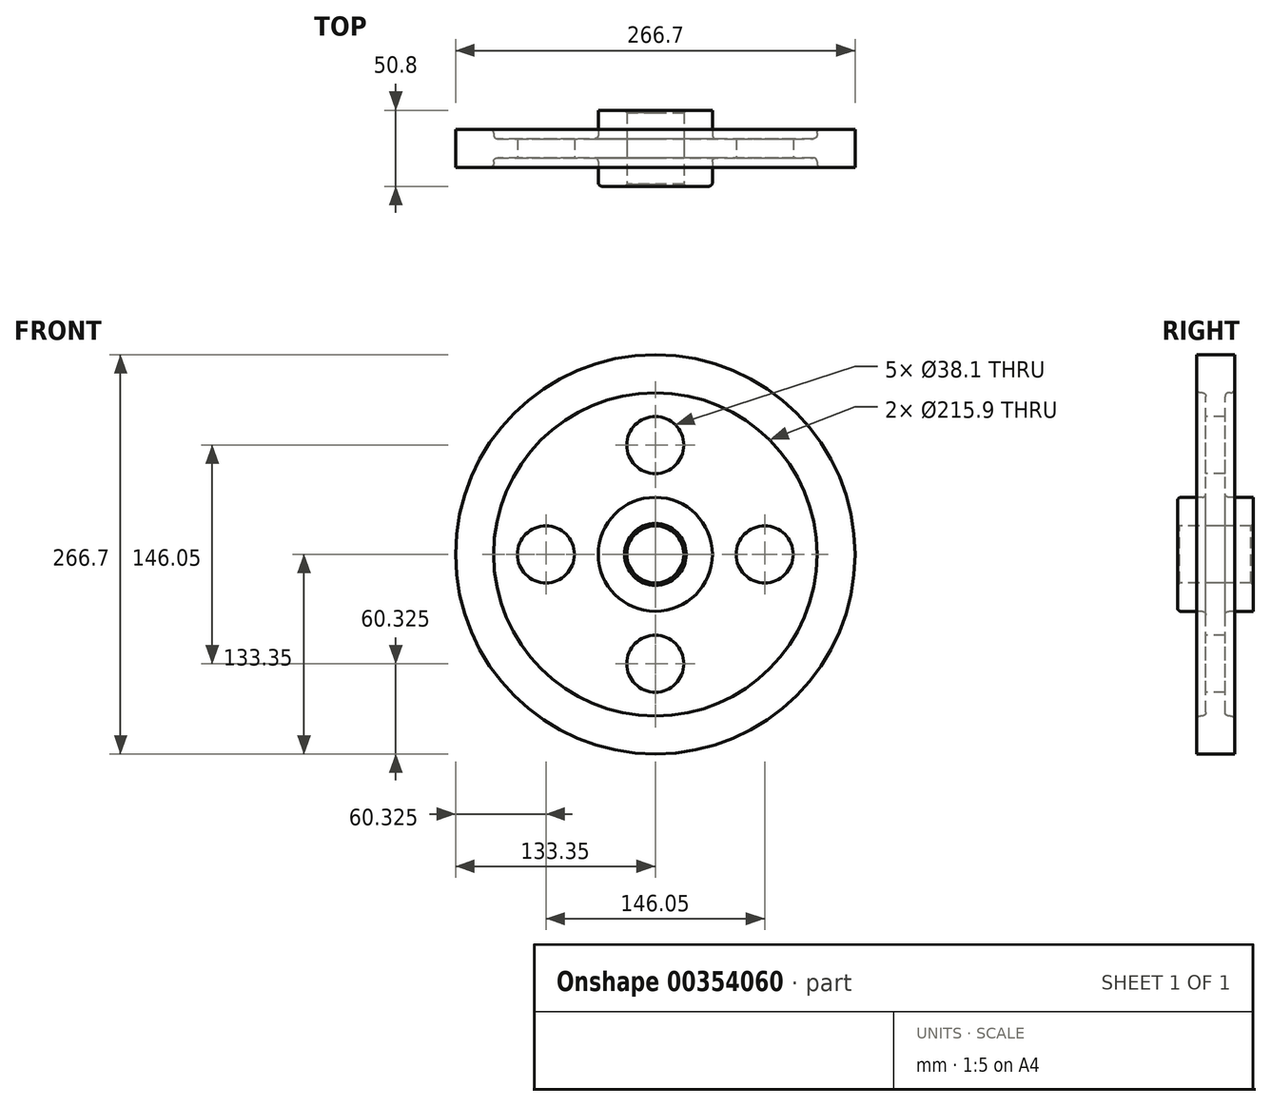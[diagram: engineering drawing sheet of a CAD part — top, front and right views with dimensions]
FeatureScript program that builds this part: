
annotation { "Feature Type Name" : "Feature", "Feature Type Description" : "" }
export const myFeature = defineFeature(function(context is Context, id is Id, definition is map)
    precondition{}
    {
        {
            var Q0;
            Q0=qCreatedBy(makeId("Right.planeOp"),FACE);
            var sketch = newSketch(context, id + "F0", { "sketchPlane" : qUnion([Q0])});
            skLineSegment(sketch, "E0", {"start": v(0, 0) * mm, "end": v(80.47, 0) * mm, "construction": true});
            skLineSegment(sketch, "E1", {"start": v(0, 0) * mm, "end": v(0, 75.13) * mm, "construction": true});
            skLineSegment(sketch, "E2.0", {"start": v(6.35, 107.95) * mm, "end": v(12.7, 107.95) * mm});
            skLineSegment(sketch, "E3.0", {"start": v(0, 133.35) * mm, "end": v(12.7, 133.35) * mm});
            skLineSegment(sketch, "E4.0", {"start": v(6.35, 38.1) * mm, "end": v(6.35, 75.13) * mm});
            skLineSegment(sketch, "E5", {"start": v(0, 75.13) * mm, "end": v(0, 133.35) * mm, "construction": true});
            skLineSegment(sketch, "E6", {"start": v(6.35, 75.13) * mm, "end": v(6.35, 107.95) * mm});
            skLineSegment(sketch, "E7.0", {"start": v(12.7, 107.95) * mm, "end": v(12.7, 133.35) * mm});
            skLineSegment(sketch, "E8.0", {"start": v(6.35, 38.1) * mm, "end": v(25.4, 38.1) * mm});
            skLineSegment(sketch, "E9", {"start": v(25.4, 19.05) * mm, "end": v(25.4, 38.1) * mm});
            skLineSegment(sketch, "E10", {"start": v(25.4, 19.05) * mm, "end": v(0, 19.05) * mm});
            skPoint(sketch, "E11.MirrorCS.end.orphan", {"position": v(12.7, 133.35) * mm});
            skLineSegment(sketch, "E12.MirrorCS", {"start": v(0, 107.95) * mm, "end": v(0, 133.35) * mm});
            skLineSegment(sketch, "E13.MirrorCS", {"start": v(0, 133.35) * mm, "end": v(-12.7, 133.35) * mm});
            skLineSegment(sketch, "E14.MirrorCS", {"start": v(-12.7, 107.95) * mm, "end": v(-12.7, 133.35) * mm});
            skLineSegment(sketch, "E15.MirrorCS", {"start": v(-6.35, 107.95) * mm, "end": v(-12.7, 107.95) * mm});
            skLineSegment(sketch, "E16.MirrorCS", {"start": v(-6.35, 75.13) * mm, "end": v(-6.35, 107.95) * mm});
            skLineSegment(sketch, "E17.MirrorCS", {"start": v(-6.35, 38.1) * mm, "end": v(-6.35, 75.13) * mm});
            skLineSegment(sketch, "E18.MirrorCS", {"start": v(-6.35, 38.1) * mm, "end": v(-25.4, 38.1) * mm});
            skLineSegment(sketch, "E19.MirrorCS", {"start": v(-25.4, 19.05) * mm, "end": v(-25.4, 38.1) * mm});
            skLineSegment(sketch, "E20.MirrorCS", {"start": v(-25.4, 19.05) * mm, "end": v(0, 19.05) * mm});
            skSolve(sketch);
        }
        {
            var Q0;
            Q0=makeQuery(id+"F0.imprint","IMPRINT",FACE,{"disambiguationData":[TD([[makeQuery(id+"F0.imprint","IMPRINT",EDGE,{"derivedFrom":sQuery(id+"F0.wireOp",EDGE,"E2.0")}),1.0]])]});
            var Q1;
            Q1=sQuery(id+"F0.wireOp",EDGE,"E0");
            revolve(context, id + "F1", {"entities" : qUnion([Q0]), "axis" : qUnion([Q1]), "revolveType" : RevolveType.FULL});
        }
        {
            var Q0;
            Q0=makeQuery(id+"F1.opRevolve","SWEPT_FACE",FACE,{"disambiguationData":[OSD([sQuery(id+"F0.wireOp",EDGE,"E19.MirrorCS")])]});
            var sketch = newSketch(context, id + "F2", { "sketchPlane" : qUnion([Q0])});
            skLineSegment(sketch, "E21", {"start": v(0, 0) * mm, "end": v(0, 73.03) * mm});
            skCircle(sketch, "E22", {"center": v(0, 73.03) * mm, "radius": 19.05 * mm});
            skCircle(sketch, "E23.1.0", {"center": v(-73.03, 0) * mm, "radius": 19.05 * mm});
            skCircle(sketch, "E23.2.0", {"center": v(0, -73.03) * mm, "radius": 19.05 * mm});
            skCircle(sketch, "E23.3.0", {"center": v(73.03, 0) * mm, "radius": 19.05 * mm});
            skPoint(sketch, "E23.center", {"position": v(0, 0) * mm});
            skSolve(sketch);
        }
        {
            var Q0;
            Q0=makeQuery(id+"F2.imprint","IMPRINT",FACE,{"disambiguationData":[TD([[makeQuery(id+"F2.imprint","IMPRINT",EDGE,{"derivedFrom":sQuery(id+"F2.wireOp",EDGE,"E23.1.0")}),1.0]])]});
            var Q1;
            Q1=makeQuery(id+"F2.imprint","IMPRINT",FACE,{"disambiguationData":[TD([[makeQuery(id+"F2.imprint","IMPRINT",EDGE,{"derivedFrom":sQuery(id+"F2.wireOp",EDGE,"E22")}),1.0]])]});
            var Q2;
            Q2=makeQuery(id+"F2.imprint","IMPRINT",FACE,{"disambiguationData":[TD([[makeQuery(id+"F2.imprint","IMPRINT",EDGE,{"derivedFrom":sQuery(id+"F2.wireOp",EDGE,"E23.3.0")}),1.0]])]});
            var Q3;
            Q3=makeQuery(id+"F2.imprint","IMPRINT",FACE,{"disambiguationData":[TD([[makeQuery(id+"F2.imprint","IMPRINT",EDGE,{"derivedFrom":sQuery(id+"F2.wireOp",EDGE,"E23.2.0")}),1.0]])]});
            extrude(context, id + "F3", {"entities" : qUnion([Q0, Q1, Q2, Q3]), "operationType" : NewBodyOperationType.REMOVE, "endBound" : BoundingType.THROUGH_ALL, "oppositeDirection" : true, "depth" : 25.4 * mm});
        }
        {
            var Q0;
            Q0=makeQuery(id+"F1.opRevolve","SWEPT_EDGE",EDGE,{"disambiguationData":[OSD([sQuery(id+"F0.wireOp",EDGE,"E15.MirrorCS"),sQuery(id+"F0.wireOp",EDGE,"E16.MirrorCS")])]});
            var Q1;
            Q1=makeQuery(id+"F1.opRevolve","SWEPT_EDGE",EDGE,{"disambiguationData":[OSD([sQuery(id+"F0.wireOp",EDGE,"E14.MirrorCS"),sQuery(id+"F0.wireOp",EDGE,"E15.MirrorCS")])]});
            var Q2;
            Q2=makeQuery(id+"F1.opRevolve","SWEPT_EDGE",EDGE,{"disambiguationData":[OSD([sQuery(id+"F0.wireOp",EDGE,"E2.0"),sQuery(id+"F0.wireOp",EDGE,"E6")])]});
            var Q3;
            Q3=makeQuery(id+"F1.opRevolve","SWEPT_EDGE",EDGE,{"disambiguationData":[OSD([sQuery(id+"F0.wireOp",EDGE,"E2.0"),sQuery(id+"F0.wireOp",EDGE,"E7.0")])]});
            var Q4;
            Q4=makeQuery(id+"F1.opRevolve","SWEPT_EDGE",EDGE,{"disambiguationData":[OSD([sQuery(id+"F0.wireOp",EDGE,"E8.0"),sQuery(id+"F0.wireOp",EDGE,"E4.0")])]});
            var Q5;
            Q5=makeQuery(id+"F1.opRevolve","SWEPT_EDGE",EDGE,{"disambiguationData":[OSD([sQuery(id+"F0.wireOp",EDGE,"E17.MirrorCS"),sQuery(id+"F0.wireOp",EDGE,"E18.MirrorCS")])]});
            var Q6;
            Q6=makeQuery(id+"F1.opRevolve","SWEPT_EDGE",EDGE,{"disambiguationData":[OSD([sQuery(id+"F0.wireOp",EDGE,"E18.MirrorCS"),sQuery(id+"F0.wireOp",EDGE,"E19.MirrorCS")])]});
            fillet(context, id + "F4", {"entities" : qUnion([Q0, Q1, Q2, Q3, Q4, Q5, Q6]), "radius" : 2.54 * mm, "tangentPropagation" : true, "allowEdgeOverflow" : false});
        }
        {
            var Q0;
            Q0=makeQuery(id+"F1.opRevolve","SWEPT_EDGE",EDGE,{"disambiguationData":[OSD([sQuery(id+"F0.wireOp",EDGE,"E19.MirrorCS"),sQuery(id+"F0.wireOp",EDGE,"E20.MirrorCS")])]});
            var Q1;
            Q1=makeQuery(id+"F1.opRevolve","SWEPT_EDGE",EDGE,{"disambiguationData":[OSD([sQuery(id+"F0.wireOp",EDGE,"E9"),sQuery(id+"F0.wireOp",EDGE,"E10")])]});
            chamfer(context, id + "F5", {"entities" : qUnion([Q0, Q1]), "width" : 1.59 * mm, "tangentPropagation" : true});
        }
    });
